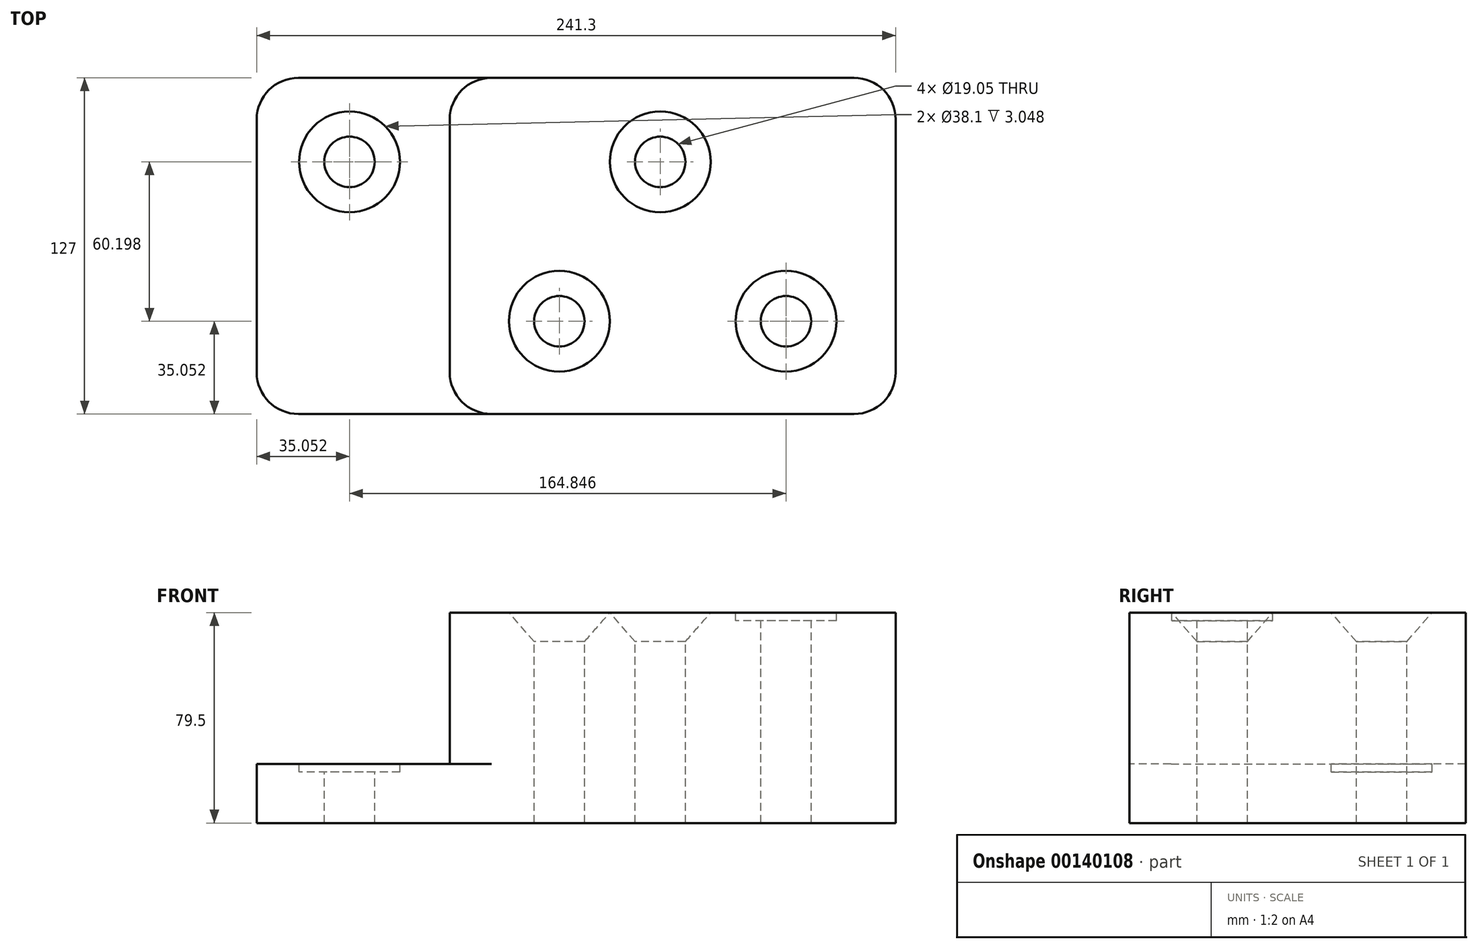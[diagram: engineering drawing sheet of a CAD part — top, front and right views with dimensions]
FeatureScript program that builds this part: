
annotation { "Feature Type Name" : "Feature", "Feature Type Description" : "" }
export const myFeature = defineFeature(function(context is Context, id is Id, definition is map)
    precondition{}
    {
        {
            var Q0;
            Q0=qCreatedBy(makeId("Front.planeOp"),FACE);
            var sketch = newSketch(context, id + "F0", { "sketchPlane" : qUnion([Q0])});
            skLineSegment(sketch, "E0", {"start": v(0, 0) * mm, "end": v(0, 22.35) * mm});
            skLineSegment(sketch, "E1", {"start": v(0, 22.35) * mm, "end": v(72.9, 22.35) * mm});
            skLineSegment(sketch, "E2", {"start": v(72.9, 22.35) * mm, "end": v(72.9, 79.5) * mm});
            skLineSegment(sketch, "E3", {"start": v(72.9, 79.5) * mm, "end": v(241.3, 79.5) * mm});
            skLineSegment(sketch, "E4", {"start": v(241.3, 79.5) * mm, "end": v(241.3, 0) * mm});
            skLineSegment(sketch, "E5", {"start": v(241.3, 0) * mm, "end": v(0, 0) * mm});
            skSolve(sketch);
        }
        {
            var Q0;
            Q0 = qSketchRegion(id + "F0", true);
            extrude(context, id + "F1", {"entities" : qUnion([Q0]), "depth" : 127 * mm});
        }
        {
            var Q0;
            Q0=makeQuery(id+"F1.opExtrude","SWEPT_FACE",FACE,{"disambiguationData":[OSD([sQuery(id+"F0.wireOp",EDGE,"E3")])]});
            var sketch = newSketch(context, id + "F2", { "sketchPlane" : qUnion([Q0])});
            skLineSegment(sketch, "E6.0", {"start": v(72.9, 0) * mm, "end": v(241.3, 0) * mm});
            skLineSegment(sketch, "E7.0", {"start": v(72.9, -127) * mm, "end": v(72.9, 0) * mm});
            skLineSegment(sketch, "E8.0", {"start": v(72.9, -127) * mm, "end": v(241.3, -127) * mm});
            skLineSegment(sketch, "E9.0", {"start": v(241.3, -127) * mm, "end": v(241.3, 0) * mm});
            skPoint(sketch, "E10", {"position": v(35.05, -31.75) * mm});
            skPoint(sketch, "E11", {"position": v(114.3, -91.95) * mm});
            skPoint(sketch, "E12", {"position": v(199.9, -91.95) * mm});
            skPoint(sketch, "E13", {"position": v(152.4, -31.75) * mm});
            skSolve(sketch);
        }
        {
            var Q0;
            Q0=sQuery(id+"F2.wireOp",VERTEX,"E13");
            var Q1;
            Q1=sQuery(id+"F2.wireOp",VERTEX,"E11");
            var Q2;
            Q2=makeQuery(id+"F1.opExtrude","SWEPT_BODY",BODY,{"disambiguationData":[OSD([sQuery(id+"F0.wireOp",EDGE,"E0"),sQuery(id+"F0.wireOp",EDGE,"E1"),sQuery(id+"F0.wireOp",EDGE,"E2"),sQuery(id+"F0.wireOp",EDGE,"E3"),sQuery(id+"F0.wireOp",EDGE,"E4"),sQuery(id+"F0.wireOp",EDGE,"E5")])]});
            hole(context, id + "F3", {"style" : HoleStyle.C_SINK, "endStyle" : HoleEndStyle.THROUGH, "holeDiameter" : 19.05 * mm, "cSinkDiameter" : 38.1 * mm, "cSinkAngle" : 82 * degree, "locations" : qUnion([Q0, Q1]), "scope" : qUnion([Q2]), "isTappedThrough" : true});
        }
        {
            var Q0;
            Q0=sQuery(id+"F2.wireOp",VERTEX,"E10");
            var Q1;
            Q1=sQuery(id+"F2.wireOp",VERTEX,"E12");
            var Q2;
            Q2=makeQuery(id+"F1.opExtrude","SWEPT_BODY",BODY,{"disambiguationData":[OSD([sQuery(id+"F0.wireOp",EDGE,"E0"),sQuery(id+"F0.wireOp",EDGE,"E1"),sQuery(id+"F0.wireOp",EDGE,"E2"),sQuery(id+"F0.wireOp",EDGE,"E3"),sQuery(id+"F0.wireOp",EDGE,"E4"),sQuery(id+"F0.wireOp",EDGE,"E5")])]});
            hole(context, id + "F4", {"style" : HoleStyle.C_BORE, "endStyle" : HoleEndStyle.THROUGH, "holeDiameter" : 19.05 * mm, "cBoreDiameter" : 38.1 * mm, "cBoreDepth" : 3.05 * mm, "locations" : qUnion([Q0, Q1]), "scope" : qUnion([Q2]), "isTappedThrough" : true});
        }
        {
            var Q0;
            Q0=makeQuery(id+"F1.opExtrude","CAP_EDGE",EDGE,{"disambiguationData":[OSD([sQuery(id+"F0.wireOp",EDGE,"E2")])],"isStart":false});
            var Q1;
            Q1=makeQuery(id+"F1.opExtrude","CAP_EDGE",EDGE,{"disambiguationData":[OSD([sQuery(id+"F0.wireOp",EDGE,"E2")])],"isStart":true});
            var Q2;
            Q2=makeQuery(id+"F1.opExtrude","CAP_EDGE",EDGE,{"disambiguationData":[OSD([sQuery(id+"F0.wireOp",EDGE,"E4")])],"isStart":false});
            var Q3;
            Q3=makeQuery(id+"F1.opExtrude","CAP_EDGE",EDGE,{"disambiguationData":[OSD([sQuery(id+"F0.wireOp",EDGE,"E4")])],"isStart":true});
            var Q4;
            Q4=makeQuery(id+"F1.opExtrude","CAP_EDGE",EDGE,{"disambiguationData":[OSD([sQuery(id+"F0.wireOp",EDGE,"E0")])],"isStart":false});
            var Q5;
            Q5=makeQuery(id+"F1.opExtrude","CAP_EDGE",EDGE,{"disambiguationData":[OSD([sQuery(id+"F0.wireOp",EDGE,"E0")])],"isStart":true});
            fillet(context, id + "F5", {"entities" : qUnion([Q0, Q1, Q2, Q3, Q4, Q5]), "radius" : 15.75 * mm, "tangentPropagation" : true, "allowEdgeOverflow" : false});
        }
    });
